# Revit family: Distanzbügel_500_FT_FS
name_source: partatom
category: Generic Models
revit_build: Autodesk Revit 2017 (Build: 20160225_1515(x64)
units: mm (PartAtom-declared; Revit-internal decimal feet)

## family parameters
Always vertical = Yes
Can host rebar = No
Cut with Voids When Loaded = No
Part Type = Normal
Room Calculation Point = No
Round Connector Dimension = Use Diameter
Shared = No
Work Plane-Based = No

## types (2) — shared parameters
Cut's number = 2
Cut's space = 450 mm  [stored 1.47638 ft]
Length = 567 mm
Length 1 = 341 mm
Length 2 = 171 mm
Length 3 = 284 mm
Manufacturer = OBO BETTERMANN
Material = Strip-galvanised
URL = http://www.obo-bettermann.com
Width = 40 mm  [stored 0.131234 ft]
zero-valued in all types: Width 1

## per-type parameters (varying)
| type | GTIN | Manufacturer Art.No. |
| DBLG 20 500 FS | 4012195239222 | 6015693 |
| DBLG 20 500 FT | 4012195239260 | 6015695 |

note: column(s) folded — value = type name in every type: Article Type

note: [stored X ft] marks values corroborated as IEEE doubles in the binary element streams (Revit-internal decimal feet)

## geometry (parser evidence)
native form markers: Sweep x2
no freeform markers — native parametric forms only
